# Revit family: Legrand_IP21_transformer_for_single_phase_hospital_rooms
name_source: partatom
category: Installations électriques
revit_build: Autodesk Revit 2018 (Build: 20170223_1515(x64)
units: mm (PartAtom-declared; Revit-internal decimal feet)

## family parameters
Basée sur le plan de construction = Non
Conserver l'orientation des annotations = Non
Cote de connecteur circulaire = Utiliser le diamètre
Couper avec des vides une fois chargée = Non
Numéro OmniClass = 23.80.00.00
Partagée = Non
Point de calcul de pièce = Non
Titre OmniClass = Electric Power and Lighting
Toujours verticalement = Oui
Type d'élément = Normal

## types (6) — shared parameters
Characteristic = Class I - IP21 - IK08
Fabricant = Legrand
General Conditions of Use = https://export.legrand.com
Primary voltage = 230V
Secondary voltage = 230V
Type of transformer = Single phase 230V/230V medium point
URL = www.legrand.com
fixing diameter = 9 mm  [stored 0.0295276 ft]

## per-type parameters (varying)
| type | 042571 | 042572, 042573, 042574 | 142575, 142576 | Insulating | Primary Cable Section | Secondary cable section | Ucc (%) | dimension A | dimension B | dimension C | empty loss | fixing F | fixing G | max totaly loss | power | weight |
| Transformer for hospital premises 142575 | Non | Non | Oui | class H | 35 mm² | 35 mm² | 3.8 | 390 mm  [stored 1.27953 ft] | 460 mm  [stored 1.50919 ft] | 380 mm | 88 W | 370 mm  [stored 1.21391 ft] | 140 mm  [stored 0.459318 ft] | 470 W | 8 kVA | 68.00 kg |
| Transformer for hospital premises 142576 | Non | Non | Oui | class H | 35 mm² | 35 mm² | 3.6 | 390 mm  [stored 1.27953 ft] | 460 mm  [stored 1.50919 ft] | 380 mm | 90 W | 370 mm  [stored 1.21391 ft] | 140 mm  [stored 0.459318 ft] | 486 W | 10 kVA | 70.00 kg |
| Transformer for hospital premises 042571 | Oui | Non | Non | class B | 16 mm² | 16 mm² | 3.1 | 320 mm  [stored 1.04987 ft] | 330 mm  [stored 1.08268 ft] | 253 mm  [stored 0.830052 ft] | 22 W | 300 mm  [stored 0.984252 ft] | 111 mm | 115 W | 3 kVA | 39.00 kg |
| Transformer for hospital premises 042572 | Non | Oui | Non | class H | 16 mm² | 16 mm² | 3.2 | 340 mm  [stored 1.11549 ft] | 410 mm  [stored 1.34514 ft] | 370 mm  [stored 1.21391 ft] | 46 W | 320 mm  [stored 1.04987 ft] | 120 mm  [stored 0.393701 ft] | 228 W | 4 kVA | 52.00 kg |
| Transformer for hospital premises 042573 | Non | Oui | Non | class H | 35 mm² | 35 mm² | 3.1 | 340 mm  [stored 1.11549 ft] | 410 mm  [stored 1.34514 ft] | 370 mm  [stored 1.21391 ft] | 64 W | 320 mm  [stored 1.04987 ft] | 150 mm | 305 W | 5 kVA | 60.00 kg |
| Transformer for hospital premises 042574 | Non | Oui | Non | class H | 35 mm² | 35 mm² | 2.8 | 340 mm  [stored 1.11549 ft] | 410 mm  [stored 1.34514 ft] | 370 mm  [stored 1.21391 ft] | 68 W | 320 mm  [stored 1.04987 ft] | 150 mm | 281 W | 6 kVA | 68.00 kg |

note: [stored X ft] marks values corroborated as IEEE doubles in the binary element streams (Revit-internal decimal feet)
